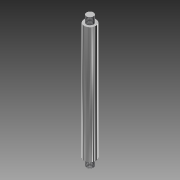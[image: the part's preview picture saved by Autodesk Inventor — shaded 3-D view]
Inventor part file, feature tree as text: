
AUTODESK INVENTOR PART (.ipt)
format: ipt  version: 2015 (Build 190159000, 159)  size: 81,920 bytes
history: native  units: mm
features: extrude x3, sketch x3, thread x2
ambient origin geometry x8: Origin, YZ Plane, XZ Plane, XY Plane, X Axis, Y Axis, Z Axis, Center Point
bodies: Solid1 (feature_tree)
feature tree (8):
  extrude  "Extrusion1"  Depth=50.0mm TaperAngle=0.0deg
  extrude  "Extrusion2"  Depth=3.0mm TaperAngle=0.0deg
  thread  "Thread1"  [1 undecoded]
  extrude  "Extrusion3"  Depth=3.0mm TaperAngle=0.0deg
  thread  "Thread2"  [1 undecoded]
  sketch  "Sketch1"  dims[d0=5.0mm d1=50.0mm d2=0.0mm]
  sketch  "Sketch2"  dims[d3=3.0mm d4=3.0mm d5=0.0mm d6=10.0mm d7=0.0mm]
  sketch  "Sketch3"  dims[d8=3.0mm d9=3.0mm d10=0.0mm d11=10.0mm d12=0.0mm]
note: 2 required parameter values undecoded (feature->parameter linkage not recoverable at this tier; creation-order binding heuristic only, values carry confidence <= 0.55)
